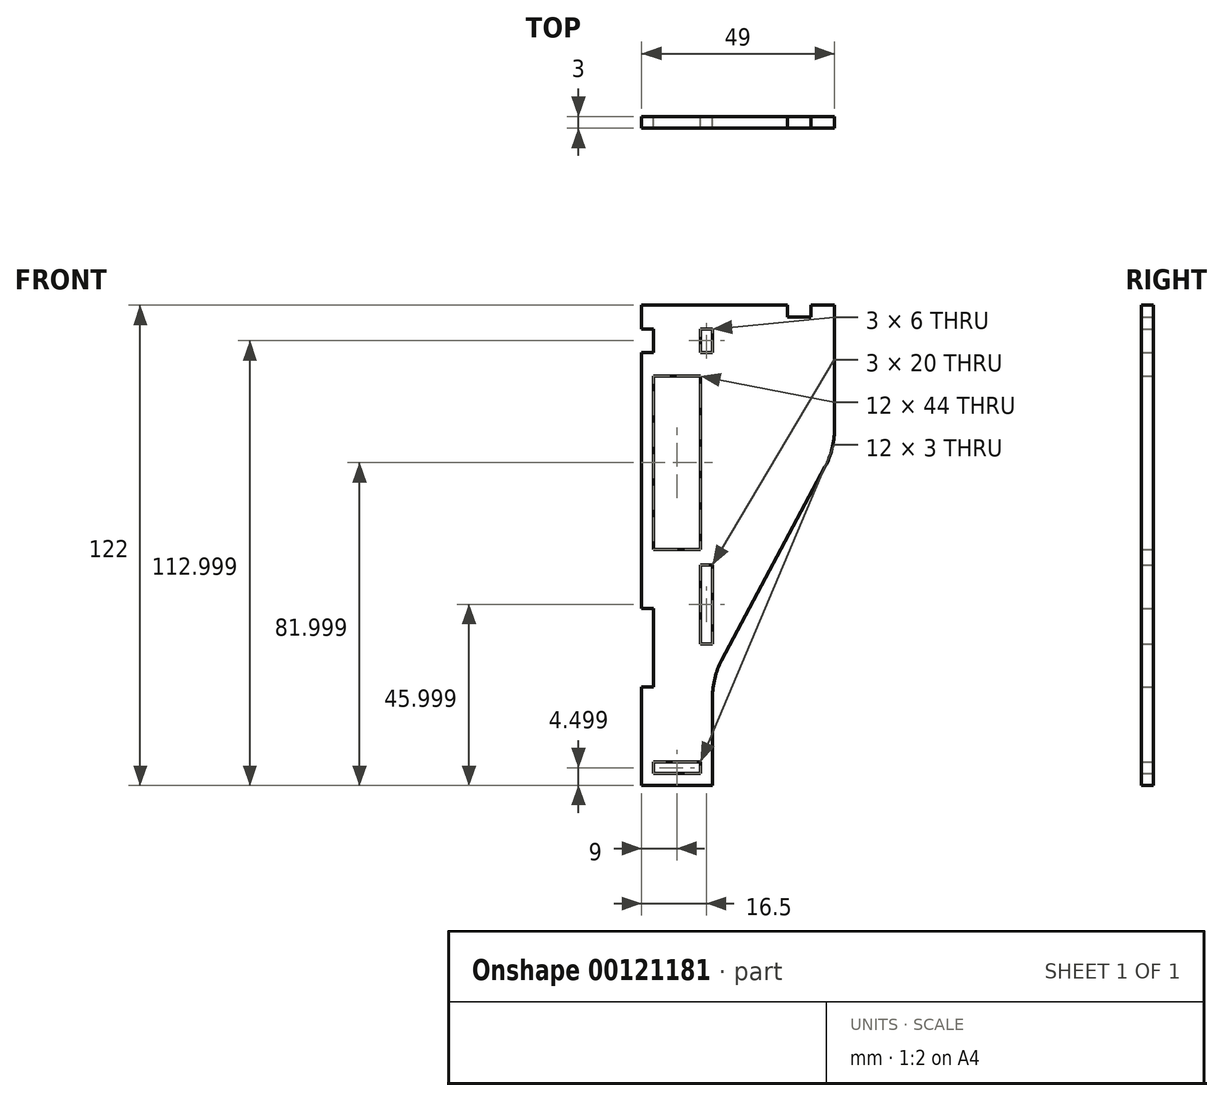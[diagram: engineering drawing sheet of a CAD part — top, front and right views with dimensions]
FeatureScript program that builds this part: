
annotation { "Feature Type Name" : "Feature", "Feature Type Description" : "" }
export const myFeature = defineFeature(function(context is Context, id is Id, definition is map)
    precondition{}
    {
        {
            var Q0;
            Q0=qCreatedBy(makeId("Front.planeOp"),FACE);
            var sketch = newSketch(context, id + "F0", { "sketchPlane" : qUnion([Q0])});
            skLineSegment(sketch, "E0", {"start": v(-184.2, 90.2) * mm, "end": v(-147.2, 90.2) * mm});
            skLineSegment(sketch, "E1", {"start": v(-135.2, 90.2) * mm, "end": v(-135.2, 58.61) * mm});
            skLineSegment(sketch, "E2", {"start": v(-137.56, 49.19) * mm, "end": v(-163.84, 0) * mm});
            skLineSegment(sketch, "E3", {"start": v(-166.2, -9.43) * mm, "end": v(-166.2, -31.8) * mm});
            skLineSegment(sketch, "E4", {"start": v(-184.2, -31.8) * mm, "end": v(-184.2, -6.8) * mm});
            skPoint(sketch, "E5.visualSharp", {"position": v(-135.2, 53.6) * mm});
            skArc(sketch, "E5.filletArc", {"start": v(-168.45, 43.63) * mm, "mid": v(-151.66, 38.93) * mm, "end": v(-137.56, 49.19) * mm, "construction": true});
            skPoint(sketch, "E6.visualSharp", {"position": v(-137.56, 49.19) * mm});
            skArc(sketch, "E6.filletArc", {"start": v(-137.56, 49.19) * mm, "mid": v(-158.74, 78.3) * mm, "end": v(-168.45, 43.63) * mm, "construction": true});
            skPoint(sketch, "E7.visualSharp", {"position": v(-166.2, -4.42) * mm});
            skArc(sketch, "E7.filletArc", {"start": v(-163.84, 0) * mm, "mid": v(-165.6, -4.57) * mm, "end": v(-166.2, -9.43) * mm});
            skLineSegment(sketch, "E8.0", {"start": v(-181.2, 28.2) * mm, "end": v(-181.2, 72.2) * mm});
            skLineSegment(sketch, "E9.0", {"start": v(-181.2, 72.2) * mm, "end": v(-169.2, 72.2) * mm});
            skLineSegment(sketch, "E10.0", {"start": v(-181.2, 28.2) * mm, "end": v(-169.2, 28.2) * mm});
            skArc(sketch, "E11", {"start": v(-137.56, 49.19) * mm, "mid": v(-135.8, 53.75) * mm, "end": v(-135.2, 58.61) * mm});
            skLineSegment(sketch, "E12.0", {"start": v(-166.2, -31.8) * mm, "end": v(-184.2, -31.8) * mm});
            skLineSegment(sketch, "E13.bottom", {"start": v(-169.2, -25.8) * mm, "end": v(-181.2, -25.8) * mm});
            skLineSegment(sketch, "E13.top", {"start": v(-169.2, -28.8) * mm, "end": v(-181.2, -28.8) * mm});
            skLineSegment(sketch, "E13.left", {"start": v(-169.2, -25.8) * mm, "end": v(-169.2, -28.8) * mm});
            skLineSegment(sketch, "E13.right", {"start": v(-181.2, -25.8) * mm, "end": v(-181.2, -28.8) * mm});
            skLineSegment(sketch, "E14", {"start": v(-184.2, 84.2) * mm, "end": v(-181.2, 84.2) * mm});
            skLineSegment(sketch, "E15", {"start": v(-181.2, 84.2) * mm, "end": v(-181.2, 78.2) * mm});
            skLineSegment(sketch, "E16", {"start": v(-181.2, 78.2) * mm, "end": v(-184.2, 78.2) * mm});
            skLineSegment(sketch, "E17", {"start": v(-184.2, 84.2) * mm, "end": v(-184.2, 90.2) * mm});
            skLineSegment(sketch, "E18", {"start": v(-184.2, 13.2) * mm, "end": v(-181.2, 13.2) * mm});
            skLineSegment(sketch, "E19", {"start": v(-181.2, 13.2) * mm, "end": v(-181.2, -6.8) * mm});
            skLineSegment(sketch, "E20", {"start": v(-181.2, -6.8) * mm, "end": v(-184.2, -6.8) * mm});
            skLineSegment(sketch, "E21", {"start": v(-184.2, 13.2) * mm, "end": v(-184.2, 78.2) * mm});
            skLineSegment(sketch, "E22", {"start": v(-169.2, 72.2) * mm, "end": v(-169.2, 28.2) * mm});
            skLineSegment(sketch, "E23.bottom", {"start": v(-169.2, 84.2) * mm, "end": v(-166.2, 84.2) * mm});
            skLineSegment(sketch, "E23.top", {"start": v(-169.2, 78.2) * mm, "end": v(-166.2, 78.2) * mm});
            skLineSegment(sketch, "E23.left", {"start": v(-169.2, 84.2) * mm, "end": v(-169.2, 78.2) * mm});
            skLineSegment(sketch, "E23.right", {"start": v(-166.2, 84.2) * mm, "end": v(-166.2, 78.2) * mm});
            skLineSegment(sketch, "E24.bottom", {"start": v(-169.2, 24.2) * mm, "end": v(-166.2, 24.2) * mm});
            skLineSegment(sketch, "E24.top", {"start": v(-169.2, 4.2) * mm, "end": v(-166.2, 4.2) * mm});
            skLineSegment(sketch, "E24.left", {"start": v(-169.2, 24.2) * mm, "end": v(-169.2, 4.2) * mm});
            skLineSegment(sketch, "E24.right", {"start": v(-166.2, 24.2) * mm, "end": v(-166.2, 4.2) * mm});
            skLineSegment(sketch, "E25.bottom", {"start": v(-147.2, 87.2) * mm, "end": v(-141.2, 87.2) * mm});
            skLineSegment(sketch, "E25.left", {"start": v(-147.2, 87.2) * mm, "end": v(-147.2, 90.2) * mm});
            skLineSegment(sketch, "E25.right", {"start": v(-141.2, 87.2) * mm, "end": v(-141.2, 90.2) * mm});
            skLineSegment(sketch, "E26", {"start": v(-141.2, 90.2) * mm, "end": v(-135.2, 90.2) * mm});
            skSolve(sketch);
        }
        {
            var Q0;
            Q0=qSketchRegion(id+"F0",true);
            extrude(context, id + "F1", {"entities" : qUnion([Q0]), "endBound" : BoundingType.SYMMETRIC, "depth" : 3 * mm});
        }
        {
            var Q0;
            {var subQ0=sQuery(id+"F0.wireOp",EDGE,"E10.0");Q0=makeQuery(id+"F0.imprint","IMPRINT",FACE,{"disambiguationData":[TD([[makeQuery(id+"F0.imprint","IMPRINT",EDGE,{"derivedFrom":subQ0}),1.0]])]});}
            var Q1;
            {var subQ3=sQuery(id+"F0.wireOp",EDGE,"E5.filletArc");var subQ5=sQuery(id+"F0.wireOp",EDGE,"E6.filletArc");var subQ6=makeQuery(id+"F0.imprint","INTERSECT",VERTEX,{"derivedFrom":[subQ3,subQ5]});Q1=makeQuery(id+"F0.imprint","IMPRINT",FACE,{"disambiguationData":[TD([[makeQuery(id+"F0.imprint","IMPRINT",EDGE,{"disambiguationData":[TD([[subQ6,-1.0]])],"derivedFrom":subQ3}),1.0]])]});}
            var Q2;
            {var subQ0=sQuery(id+"F0.wireOp",EDGE,"E9.0");var subQ1=sQuery(id+"F0.wireOp",EDGE,"E6.filletArc");var subQ2=makeQuery(id+"F0.imprint","INTERSECT",VERTEX,{"derivedFrom":[subQ1,subQ0]});Q2=makeQuery(id+"F0.imprint","IMPRINT",FACE,{"disambiguationData":[TD([[makeQuery(id+"F0.imprint","IMPRINT",EDGE,{"disambiguationData":[TD([[subQ2,-1.0]])],"derivedFrom":subQ1}),-1.0]])]});}
            extrude(context, id + "F2", {"entities" : qUnion([Q0, Q1, Q2]), "operationType" : NewBodyOperationType.REMOVE, "endBound" : BoundingType.SYMMETRIC, "oppositeDirection" : true, "depth" : 3 * mm});
        }
        {
            var Q0;
            Q0=makeQuery(id+"F0.imprint","IMPRINT",FACE,{"disambiguationData":[TD([[makeQuery(id+"F0.imprint","IMPRINT",EDGE,{"derivedFrom":sQuery(id+"F0.wireOp",EDGE,"E13.bottom")}),1.0]])]});
            extrude(context, id + "F3", {"entities" : qUnion([Q0]), "operationType" : NewBodyOperationType.REMOVE, "endBound" : BoundingType.SYMMETRIC, "oppositeDirection" : true, "depth" : 3 * mm});
        }
    });
